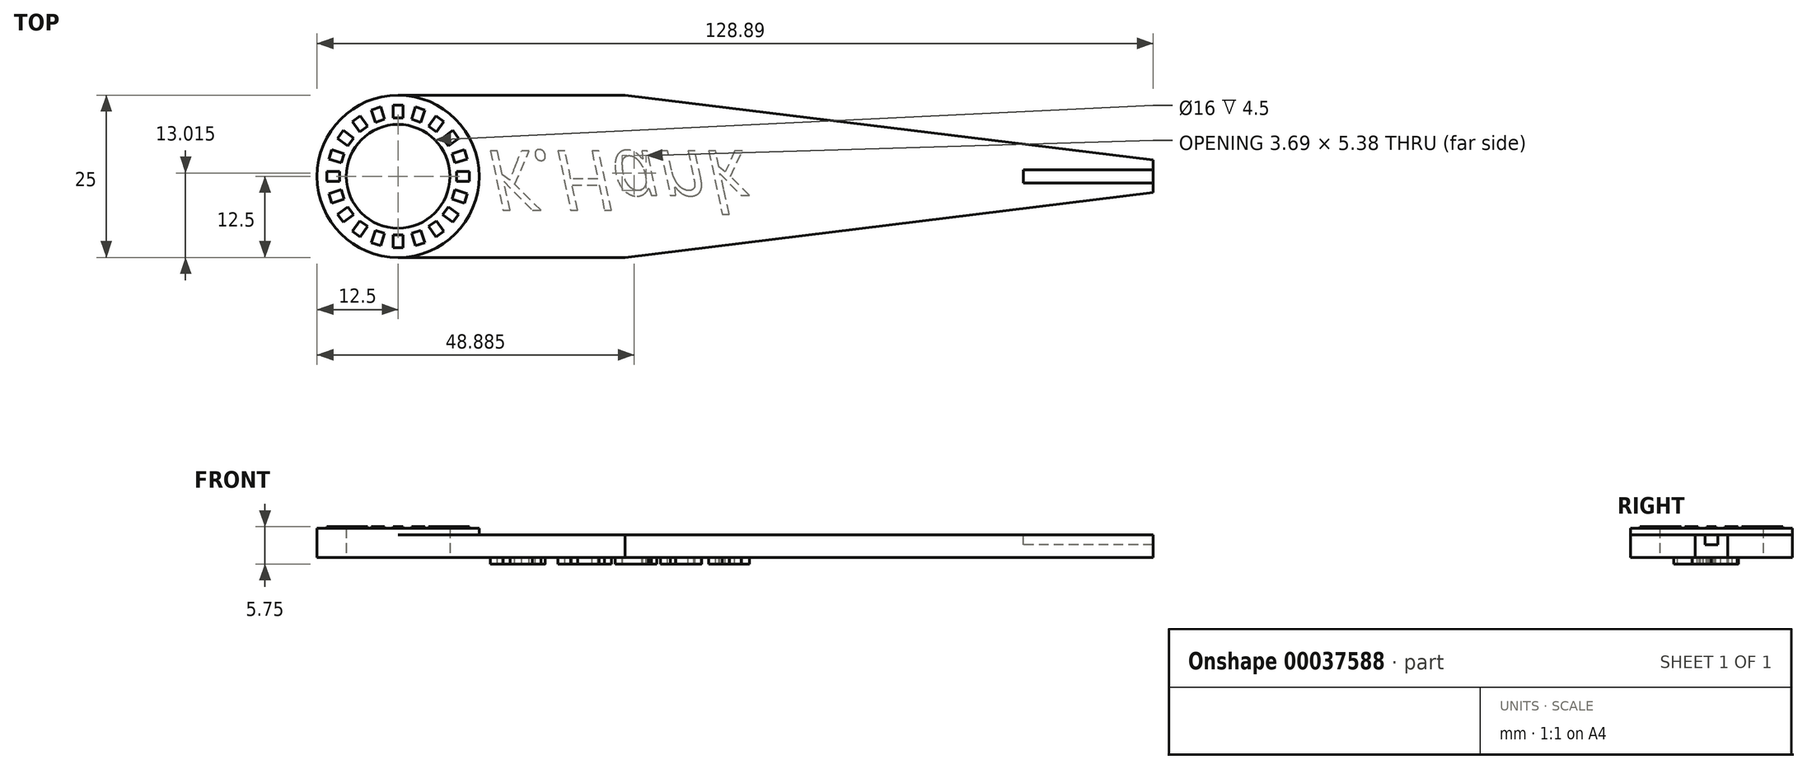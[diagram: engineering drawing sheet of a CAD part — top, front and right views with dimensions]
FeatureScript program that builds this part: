
annotation { "Feature Type Name" : "Feature", "Feature Type Description" : "" }
export const myFeature = defineFeature(function(context is Context, id is Id, definition is map)
    precondition{}
    {
        {
            var Q0;
            Q0=qCreatedBy(makeId("Top.planeOp"),FACE);
            var sketch = newSketch(context, id + "F0", { "sketchPlane" : qUnion([Q0])});
            skCircle(sketch, "E0", {"center": v(0, 0) * mm, "radius": 8 * mm});
            skCircle(sketch, "E1", {"center": v(0, 0) * mm, "radius": 12.5 * mm});
            skLineSegment(sketch, "E2", {"start": v(0, 12.5) * mm, "end": v(35, 12.5) * mm});
            skLineSegment(sketch, "E3", {"start": v(0, 0) * mm, "end": v(35.83, 0) * mm, "construction": true});
            skLineSegment(sketch, "E4.MirrorCS", {"start": v(0, -12.5) * mm, "end": v(35, -12.5) * mm});
            skLineSegment(sketch, "E5", {"start": v(35, -12.5) * mm, "end": v(61.03, -12.5) * mm, "construction": true});
            skLineSegment(sketch, "E6", {"start": v(35, -12.5) * mm, "end": v(116.39, -2.5) * mm});
            skLineSegment(sketch, "E7.MirrorCS", {"start": v(35, 12.5) * mm, "end": v(116.39, 2.5) * mm});
            skLineSegment(sketch, "E8", {"start": v(116.39, -2.5) * mm, "end": v(116.39, 2.5) * mm});
            skSolve(sketch);
        }
        {
            var Q0;
            Q0 = qSketchRegion(id + "F0", true);
            extrude(context, id + "F1", {"entities" : qUnion([Q0]), "depth" : 3.5 * mm});
        }
        {
            var Q0;
            Q0=makeQuery(id+"F1.opExtrude","CAP_FACE",FACE,{"disambiguationData":[OSD([sQuery(id+"F0.wireOp",EDGE,"E0"),sQuery(id+"F0.wireOp",EDGE,"E1"),sQuery(id+"F0.wireOp",EDGE,"E2"),sQuery(id+"F0.wireOp",EDGE,"E4.MirrorCS"),sQuery(id+"F0.wireOp",EDGE,"E6"),sQuery(id+"F0.wireOp",EDGE,"E7.MirrorCS"),sQuery(id+"F0.wireOp",EDGE,"E8")])],"isStart":false});
            var sketch = newSketch(context, id + "F2", { "sketchPlane" : qUnion([Q0])});
            skCircle(sketch, "E9", {"center": v(0, 0) * mm, "radius": 12.5 * mm});
            skCircle(sketch, "E10", {"center": v(0, 0) * mm, "radius": 8 * mm});
            skSolve(sketch);
        }
        {
            var Q0;
            Q0 = qSketchRegion(id + "F2", true);
            extrude(context, id + "F3", {"entities" : qUnion([Q0]), "operationType" : NewBodyOperationType.ADD, "depth" : 1 * mm});
        }
        {
            var Q0;
            Q0=makeQuery(id+"F3.opExtrude","CAP_FACE",FACE,{"disambiguationData":[OSD([sQuery(id+"F2.wireOp",EDGE,"E9"),sQuery(id+"F2.wireOp",EDGE,"E10")])],"isStart":false});
            var sketch = newSketch(context, id + "F4", { "sketchPlane" : qUnion([Q0])});
            skLineSegment(sketch, "E11.bottom", {"start": v(-0.75, 11) * mm, "end": v(0.75, 11) * mm});
            skLineSegment(sketch, "E11.top", {"start": v(-0.75, 9) * mm, "end": v(0.75, 9) * mm});
            skLineSegment(sketch, "E11.left", {"start": v(-0.75, 11) * mm, "end": v(-0.75, 9) * mm});
            skLineSegment(sketch, "E11.right", {"start": v(0.75, 11) * mm, "end": v(0.75, 9) * mm});
            skPoint(sketch, "E12", {"position": v(0, 8) * mm});
            skLineSegment(sketch, "E13.1.0", {"start": v(-2.69, 10.7) * mm, "end": v(-2.07, 8.8) * mm});
            skLineSegment(sketch, "E13.1.1", {"start": v(-4.11, 10.23) * mm, "end": v(-2.69, 10.7) * mm});
            skLineSegment(sketch, "E13.1.2", {"start": v(-4.11, 10.23) * mm, "end": v(-3.5, 8.33) * mm});
            skLineSegment(sketch, "E13.1.3", {"start": v(-3.5, 8.33) * mm, "end": v(-2.07, 8.8) * mm});
            skLineSegment(sketch, "E13.2.0", {"start": v(-5.86, 9.34) * mm, "end": v(-4.68, 7.72) * mm});
            skLineSegment(sketch, "E13.2.1", {"start": v(-7.07, 8.46) * mm, "end": v(-5.86, 9.34) * mm});
            skLineSegment(sketch, "E13.2.2", {"start": v(-7.07, 8.46) * mm, "end": v(-5.9, 6.84) * mm});
            skLineSegment(sketch, "E13.2.3", {"start": v(-5.9, 6.84) * mm, "end": v(-4.68, 7.72) * mm});
            skLineSegment(sketch, "E13.3.0", {"start": v(-8.46, 7.07) * mm, "end": v(-6.84, 5.9) * mm});
            skLineSegment(sketch, "E13.3.1", {"start": v(-9.34, 5.86) * mm, "end": v(-8.46, 7.07) * mm});
            skLineSegment(sketch, "E13.3.2", {"start": v(-9.34, 5.86) * mm, "end": v(-7.72, 4.68) * mm});
            skLineSegment(sketch, "E13.3.3", {"start": v(-7.72, 4.68) * mm, "end": v(-6.84, 5.9) * mm});
            skLineSegment(sketch, "E13.4.0", {"start": v(-10.23, 4.11) * mm, "end": v(-8.33, 3.5) * mm});
            skLineSegment(sketch, "E13.4.1", {"start": v(-10.7, 2.69) * mm, "end": v(-10.23, 4.11) * mm});
            skLineSegment(sketch, "E13.4.2", {"start": v(-10.7, 2.69) * mm, "end": v(-8.8, 2.07) * mm});
            skLineSegment(sketch, "E13.4.3", {"start": v(-8.8, 2.07) * mm, "end": v(-8.33, 3.5) * mm});
            skLineSegment(sketch, "E13.5.0", {"start": v(-11, 0.75) * mm, "end": v(-9, 0.75) * mm});
            skLineSegment(sketch, "E13.5.1", {"start": v(-11, -0.75) * mm, "end": v(-11, 0.75) * mm});
            skLineSegment(sketch, "E13.5.2", {"start": v(-11, -0.75) * mm, "end": v(-9, -0.75) * mm});
            skLineSegment(sketch, "E13.5.3", {"start": v(-9, -0.75) * mm, "end": v(-9, 0.75) * mm});
            skLineSegment(sketch, "E13.6.0", {"start": v(-10.7, -2.69) * mm, "end": v(-8.8, -2.07) * mm});
            skLineSegment(sketch, "E13.6.1", {"start": v(-10.23, -4.11) * mm, "end": v(-10.7, -2.69) * mm});
            skLineSegment(sketch, "E13.6.2", {"start": v(-10.23, -4.11) * mm, "end": v(-8.33, -3.5) * mm});
            skLineSegment(sketch, "E13.6.3", {"start": v(-8.33, -3.5) * mm, "end": v(-8.8, -2.07) * mm});
            skLineSegment(sketch, "E13.7.0", {"start": v(-9.34, -5.86) * mm, "end": v(-7.72, -4.68) * mm});
            skLineSegment(sketch, "E13.7.1", {"start": v(-8.46, -7.07) * mm, "end": v(-9.34, -5.86) * mm});
            skLineSegment(sketch, "E13.7.2", {"start": v(-8.46, -7.07) * mm, "end": v(-6.84, -5.9) * mm});
            skLineSegment(sketch, "E13.7.3", {"start": v(-6.84, -5.9) * mm, "end": v(-7.72, -4.68) * mm});
            skLineSegment(sketch, "E13.8.0", {"start": v(-7.07, -8.46) * mm, "end": v(-5.9, -6.84) * mm});
            skLineSegment(sketch, "E13.8.1", {"start": v(-5.86, -9.34) * mm, "end": v(-7.07, -8.46) * mm});
            skLineSegment(sketch, "E13.8.2", {"start": v(-5.86, -9.34) * mm, "end": v(-4.68, -7.72) * mm});
            skLineSegment(sketch, "E13.8.3", {"start": v(-4.68, -7.72) * mm, "end": v(-5.9, -6.84) * mm});
            skLineSegment(sketch, "E13.9.0", {"start": v(-4.11, -10.23) * mm, "end": v(-3.5, -8.33) * mm});
            skLineSegment(sketch, "E13.9.1", {"start": v(-2.69, -10.7) * mm, "end": v(-4.11, -10.23) * mm});
            skLineSegment(sketch, "E13.9.2", {"start": v(-2.69, -10.7) * mm, "end": v(-2.07, -8.8) * mm});
            skLineSegment(sketch, "E13.9.3", {"start": v(-2.07, -8.8) * mm, "end": v(-3.5, -8.33) * mm});
            skLineSegment(sketch, "E13.10.0", {"start": v(-0.75, -11) * mm, "end": v(-0.75, -9) * mm});
            skLineSegment(sketch, "E13.10.1", {"start": v(0.75, -11) * mm, "end": v(-0.75, -11) * mm});
            skLineSegment(sketch, "E13.10.2", {"start": v(0.75, -11) * mm, "end": v(0.75, -9) * mm});
            skLineSegment(sketch, "E13.10.3", {"start": v(0.75, -9) * mm, "end": v(-0.75, -9) * mm});
            skLineSegment(sketch, "E13.11.0", {"start": v(2.69, -10.7) * mm, "end": v(2.07, -8.8) * mm});
            skLineSegment(sketch, "E13.11.1", {"start": v(4.11, -10.23) * mm, "end": v(2.69, -10.7) * mm});
            skLineSegment(sketch, "E13.11.2", {"start": v(4.11, -10.23) * mm, "end": v(3.5, -8.33) * mm});
            skLineSegment(sketch, "E13.11.3", {"start": v(3.5, -8.33) * mm, "end": v(2.07, -8.8) * mm});
            skLineSegment(sketch, "E13.12.0", {"start": v(5.86, -9.34) * mm, "end": v(4.68, -7.72) * mm});
            skLineSegment(sketch, "E13.12.1", {"start": v(7.07, -8.46) * mm, "end": v(5.86, -9.34) * mm});
            skLineSegment(sketch, "E13.12.2", {"start": v(7.07, -8.46) * mm, "end": v(5.9, -6.84) * mm});
            skLineSegment(sketch, "E13.12.3", {"start": v(5.9, -6.84) * mm, "end": v(4.68, -7.72) * mm});
            skLineSegment(sketch, "E13.13.0", {"start": v(8.46, -7.07) * mm, "end": v(6.84, -5.9) * mm});
            skLineSegment(sketch, "E13.13.1", {"start": v(9.34, -5.86) * mm, "end": v(8.46, -7.07) * mm});
            skLineSegment(sketch, "E13.13.2", {"start": v(9.34, -5.86) * mm, "end": v(7.72, -4.68) * mm});
            skLineSegment(sketch, "E13.13.3", {"start": v(7.72, -4.68) * mm, "end": v(6.84, -5.9) * mm});
            skLineSegment(sketch, "E13.14.0", {"start": v(10.23, -4.11) * mm, "end": v(8.33, -3.5) * mm});
            skLineSegment(sketch, "E13.14.1", {"start": v(10.7, -2.69) * mm, "end": v(10.23, -4.11) * mm});
            skLineSegment(sketch, "E13.14.2", {"start": v(10.7, -2.69) * mm, "end": v(8.8, -2.07) * mm});
            skLineSegment(sketch, "E13.14.3", {"start": v(8.8, -2.07) * mm, "end": v(8.33, -3.5) * mm});
            skLineSegment(sketch, "E13.15.0", {"start": v(11, -0.75) * mm, "end": v(9, -0.75) * mm});
            skLineSegment(sketch, "E13.15.1", {"start": v(11, 0.75) * mm, "end": v(11, -0.75) * mm});
            skLineSegment(sketch, "E13.15.2", {"start": v(11, 0.75) * mm, "end": v(9, 0.75) * mm});
            skLineSegment(sketch, "E13.15.3", {"start": v(9, 0.75) * mm, "end": v(9, -0.75) * mm});
            skLineSegment(sketch, "E13.16.0", {"start": v(10.7, 2.69) * mm, "end": v(8.8, 2.07) * mm});
            skLineSegment(sketch, "E13.16.1", {"start": v(10.23, 4.11) * mm, "end": v(10.7, 2.69) * mm});
            skLineSegment(sketch, "E13.16.2", {"start": v(10.23, 4.11) * mm, "end": v(8.33, 3.5) * mm});
            skLineSegment(sketch, "E13.16.3", {"start": v(8.33, 3.5) * mm, "end": v(8.8, 2.07) * mm});
            skLineSegment(sketch, "E13.17.0", {"start": v(9.34, 5.86) * mm, "end": v(7.72, 4.68) * mm});
            skLineSegment(sketch, "E13.17.1", {"start": v(8.46, 7.07) * mm, "end": v(9.34, 5.86) * mm});
            skLineSegment(sketch, "E13.17.2", {"start": v(8.46, 7.07) * mm, "end": v(6.84, 5.9) * mm});
            skLineSegment(sketch, "E13.17.3", {"start": v(6.84, 5.9) * mm, "end": v(7.72, 4.68) * mm});
            skLineSegment(sketch, "E13.18.0", {"start": v(7.07, 8.46) * mm, "end": v(5.9, 6.84) * mm});
            skLineSegment(sketch, "E13.18.1", {"start": v(5.86, 9.34) * mm, "end": v(7.07, 8.46) * mm});
            skLineSegment(sketch, "E13.18.2", {"start": v(5.86, 9.34) * mm, "end": v(4.68, 7.72) * mm});
            skLineSegment(sketch, "E13.18.3", {"start": v(4.68, 7.72) * mm, "end": v(5.9, 6.84) * mm});
            skLineSegment(sketch, "E13.19.0", {"start": v(4.11, 10.23) * mm, "end": v(3.5, 8.33) * mm});
            skLineSegment(sketch, "E13.19.1", {"start": v(2.69, 10.7) * mm, "end": v(4.11, 10.23) * mm});
            skLineSegment(sketch, "E13.19.2", {"start": v(2.69, 10.7) * mm, "end": v(2.07, 8.8) * mm});
            skLineSegment(sketch, "E13.19.3", {"start": v(2.07, 8.8) * mm, "end": v(3.5, 8.33) * mm});
            skPoint(sketch, "E13.center", {"position": v(0, 0) * mm});
            skSolve(sketch);
        }
        {
            var Q0;
            Q0 = qSketchRegion(id + "F4", true);
            extrude(context, id + "F5", {"entities" : qUnion([Q0]), "operationType" : NewBodyOperationType.ADD, "depth" : .25 * mm});
        }
        {
            var Q0;
            Q0=makeQuery(id+"F1.opExtrude","CAP_FACE",FACE,{"disambiguationData":[OSD([sQuery(id+"F0.wireOp",EDGE,"E0"),sQuery(id+"F0.wireOp",EDGE,"E1"),sQuery(id+"F0.wireOp",EDGE,"E2"),sQuery(id+"F0.wireOp",EDGE,"E4.MirrorCS"),sQuery(id+"F0.wireOp",EDGE,"E6"),sQuery(id+"F0.wireOp",EDGE,"E7.MirrorCS"),sQuery(id+"F0.wireOp",EDGE,"E8")])],"isStart":false});
            var sketch = newSketch(context, id + "F6", { "sketchPlane" : qUnion([Q0])});
            skLineSegment(sketch, "E14.bottom", {"start": v(116.39, 1) * mm, "end": v(96.39, 1) * mm});
            skLineSegment(sketch, "E14.top", {"start": v(116.39, -1) * mm, "end": v(96.39, -1) * mm});
            skLineSegment(sketch, "E14.left", {"start": v(116.39, 1) * mm, "end": v(116.39, -1) * mm});
            skLineSegment(sketch, "E14.right", {"start": v(96.39, 1) * mm, "end": v(96.39, -1) * mm});
            skSolve(sketch);
        }
        {
            var Q0;
            Q0 = qSketchRegion(id + "F6", true);
            extrude(context, id + "F7", {"entities" : qUnion([Q0]), "operationType" : NewBodyOperationType.REMOVE, "oppositeDirection" : true, "depth" : 1.5 * mm});
        }
        {
            var Q0;
            Q0=makeQuery(id+"F1.opExtrude","CAP_FACE",FACE,{"disambiguationData":[OSD([sQuery(id+"F0.wireOp",EDGE,"E0"),sQuery(id+"F0.wireOp",EDGE,"E1"),sQuery(id+"F0.wireOp",EDGE,"E2"),sQuery(id+"F0.wireOp",EDGE,"E4.MirrorCS"),sQuery(id+"F0.wireOp",EDGE,"E6"),sQuery(id+"F0.wireOp",EDGE,"E7.MirrorCS"),sQuery(id+"F0.wireOp",EDGE,"E8")])],"isStart":true});
            var sketch = newSketch(context, id + "F8", { "sketchPlane" : qUnion([Q0])});
            skText(sketch, "E15", { "text": "K.Hank", "fontName": "OpenSans-Italic.ttf"});
            const initialGuessF8  = {"E15": [0.0137, -0.00395, 1, 0, 0.00926]};
            skSetInitialGuess(sketch, initialGuessF8);
            skSolve(sketch);
        }
        {
            var Q0;
            Q0 = qSketchRegion(id + "F8", true);
            extrude(context, id + "F9", {"entities" : qUnion([Q0]), "depth" : 1 * mm});
        }
    });
